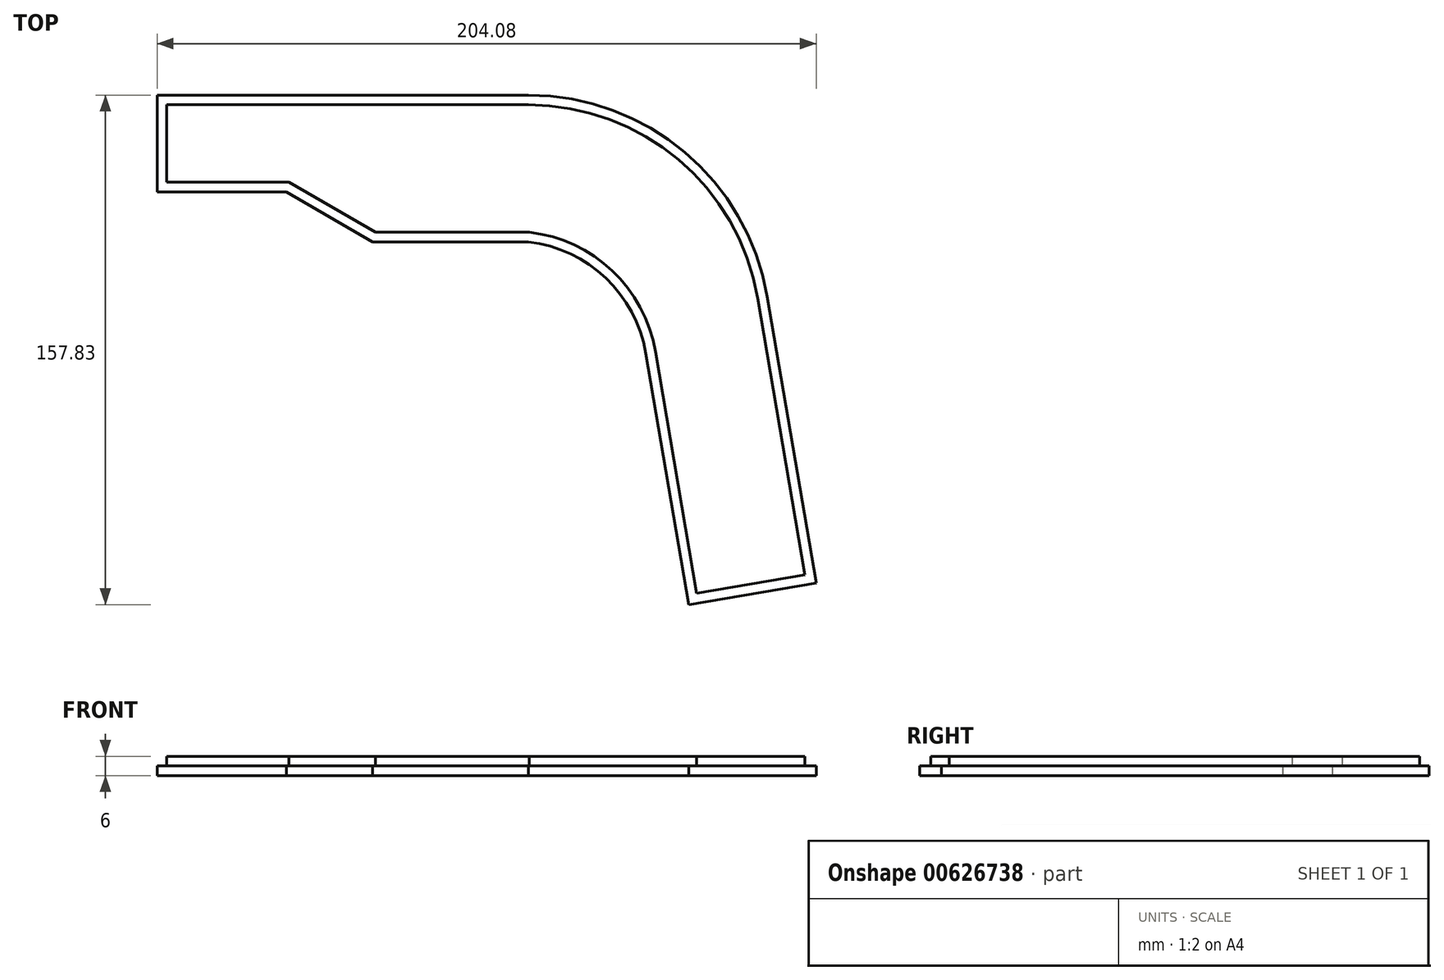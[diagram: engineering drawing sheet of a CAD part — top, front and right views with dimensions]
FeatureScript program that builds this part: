
annotation { "Feature Type Name" : "Feature", "Feature Type Description" : "" }
export const myFeature = defineFeature(function(context is Context, id is Id, definition is map)
    precondition{}
    {
        {
            var Q0;
            Q0=qCreatedBy(makeId("Top.planeOp"),FACE);
            var sketch = newSketch(context, id + "F0", { "sketchPlane" : qUnion([Q0])});
            skLineSegment(sketch, "E0", {"start": v(-134.82, 85.58) * mm, "end": v(-19.82, 85.58) * mm});
            skLineSegment(sketch, "E1", {"start": v(-134.82, 85.58) * mm, "end": v(-134.82, 55.58) * mm});
            skLineSegment(sketch, "E2", {"start": v(-134.82, 55.58) * mm, "end": v(-94.82, 55.58) * mm});
            skArc(sketch, "E3", {"start": v(54.12, 23.2) * mm, "mid": v(28.55, 67.9) * mm, "end": v(-19.82, 85.58) * mm});
            skLineSegment(sketch, "E4", {"start": v(54.12, 23.2) * mm, "end": v(69.26, -65.52) * mm});
            skLineSegment(sketch, "E5", {"start": v(69.26, -65.52) * mm, "end": v(29.83, -72.25) * mm});
            skLineSegment(sketch, "E6", {"start": v(-94.82, 55.58) * mm, "end": v(-68.08, 40.14) * mm});
            skLineSegment(sketch, "E7", {"start": v(-68.08, 40.14) * mm, "end": v(-19.82, 40.14) * mm});
            skLineSegment(sketch, "E8", {"start": v(29.83, -72.25) * mm, "end": v(16.54, 5.6) * mm});
            skArc(sketch, "E9", {"start": v(16.54, 5.6) * mm, "mid": v(4.1, 28.92) * mm, "end": v(-19.82, 40.14) * mm});
            skSolve(sketch);
        }
        {
            var Q0;
            Q0=makeQuery(id+"F0.imprint","IMPRINT",FACE,{"disambiguationData":[TD([[makeQuery(id+"F0.imprint","IMPRINT",EDGE,{"derivedFrom":sQuery(id+"F0.wireOp",EDGE,"E0")}),-1.0]])]});
            extrude(context, id + "F1", {"entities" : qUnion([Q0]), "depth" : 3 * mm, "offsetDistance" : 25 * mm});
        }
        {
            var Q0;
            Q0=makeQuery(id+"F1.opExtrude","CAP_FACE",FACE,{"disambiguationData":[OSD([sQuery(id+"F0.wireOp",EDGE,"E0"),sQuery(id+"F0.wireOp",EDGE,"E1"),sQuery(id+"F0.wireOp",EDGE,"E2"),sQuery(id+"F0.wireOp",EDGE,"E3"),sQuery(id+"F0.wireOp",EDGE,"E4"),sQuery(id+"F0.wireOp",EDGE,"E5"),sQuery(id+"F0.wireOp",EDGE,"E6"),sQuery(id+"F0.wireOp",EDGE,"E7"),sQuery(id+"F0.wireOp",EDGE,"E8"),sQuery(id+"F0.wireOp",EDGE,"E9")])],"isStart":false});
            var sketch = newSketch(context, id + "F2", { "sketchPlane" : qUnion([Q0])});
            skLineSegment(sketch, "E10.0", {"start": v(-67.27, 43.14) * mm, "end": v(-19.64, 43.14) * mm});
            skLineSegment(sketch, "E10.1", {"start": v(-94.01, 58.58) * mm, "end": v(-67.27, 43.14) * mm});
            skArc(sketch, "E10.2", {"start": v(-19.64, 43.14) * mm, "mid": v(6.1, 31.16) * mm, "end": v(19.5, 6.11) * mm});
            skLineSegment(sketch, "E10.3", {"start": v(-131.82, 58.58) * mm, "end": v(-94.01, 58.58) * mm});
            skLineSegment(sketch, "E10.4", {"start": v(-131.82, 82.58) * mm, "end": v(-131.82, 58.58) * mm});
            skLineSegment(sketch, "E10.5", {"start": v(-19.82, 82.58) * mm, "end": v(-131.82, 82.58) * mm});
            skLineSegment(sketch, "E10.6", {"start": v(19.5, 6.11) * mm, "end": v(32.28, -68.79) * mm});
            skLineSegment(sketch, "E10.7", {"start": v(32.28, -68.79) * mm, "end": v(65.8, -63.07) * mm});
            skLineSegment(sketch, "E10.8", {"start": v(65.8, -63.07) * mm, "end": v(51.16, 22.7) * mm});
            skArc(sketch, "E10.9", {"start": v(51.16, 22.7) * mm, "mid": v(26.62, 65.6) * mm, "end": v(-19.82, 82.58) * mm});
            skSolve(sketch);
        }
        {
            var Q0;
            Q0=makeQuery(id+"F2.imprint","IMPRINT",FACE,{"disambiguationData":[TD([[makeQuery(id+"F2.imprint","IMPRINT",EDGE,{"derivedFrom":sQuery(id+"F2.wireOp",EDGE,"E10.0")}),1.0]])]});
            extrude(context, id + "F3", {"entities" : qUnion([Q0]), "operationType" : NewBodyOperationType.ADD, "depth" : 3 * mm, "offsetDistance" : 25 * mm});
        }
    });
